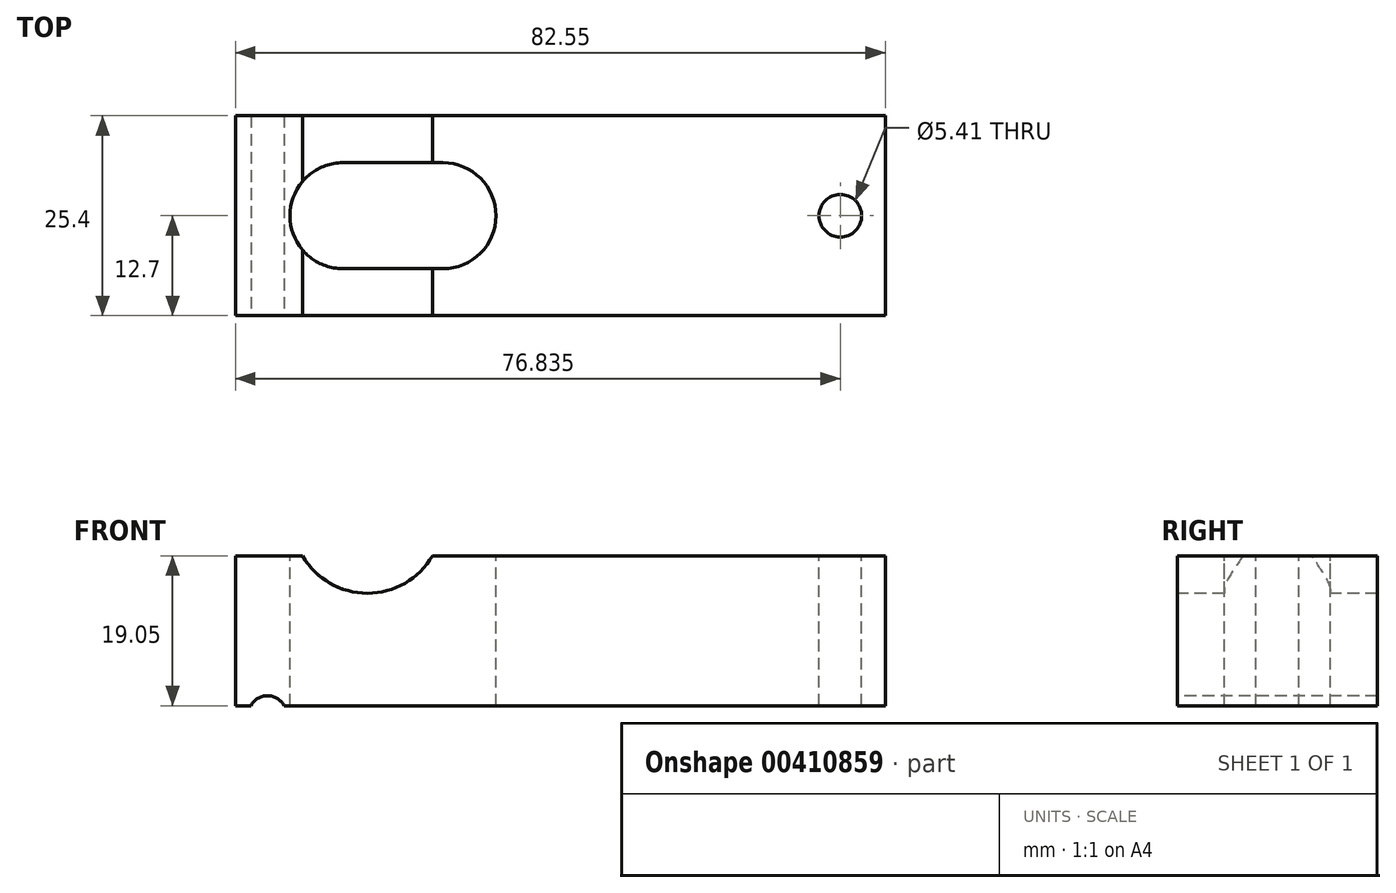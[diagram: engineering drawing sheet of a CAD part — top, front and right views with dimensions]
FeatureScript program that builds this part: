
annotation { "Feature Type Name" : "Feature", "Feature Type Description" : "" }
export const myFeature = defineFeature(function(context is Context, id is Id, definition is map)
    precondition{}
    {
        {
            var Q0;
            Q0=qCreatedBy(makeId("Front.planeOp"),FACE);
            var sketch = newSketch(context, id + "F0", { "sketchPlane" : qUnion([Q0])});
            skLineSegment(sketch, "E0.bottom", {"start": v(0, 0) * mm, "end": v(82.55, 0) * mm});
            skLineSegment(sketch, "E0.top", {"start": v(0, -19.05) * mm, "end": v(82.55, -19.05) * mm});
            skLineSegment(sketch, "E0.left", {"start": v(0, 0) * mm, "end": v(0, -19.05) * mm});
            skLineSegment(sketch, "E0.right", {"start": v(82.55, 0) * mm, "end": v(82.55, -19.05) * mm});
            skSolve(sketch);
        }
        {
            var Q0;
            Q0 = qSketchRegion(id + "F0", true);
            extrude(context, id + "F1", {"entities" : qUnion([Q0]), "depth" : 25.4 * mm});
        }
        {
            var Q0;
            Q0=makeQuery(id+"F1.opExtrude","SWEPT_FACE",FACE,{"disambiguationData":[OSD([sQuery(id+"F0.wireOp",EDGE,"E0.bottom")])]});
            var sketch = newSketch(context, id + "F2", { "sketchPlane" : qUnion([Q0])});
            skLineSegment(sketch, "E1", {"start": v(13.65, -12.7) * mm, "end": v(26.35, -12.7) * mm, "construction": true});
            skLineSegment(sketch, "E2", {"start": v(13.65, -5.97) * mm, "end": v(26.35, -5.97) * mm});
            skLineSegment(sketch, "E3", {"start": v(13.65, -19.43) * mm, "end": v(26.35, -19.43) * mm});
            skArc(sketch, "E4", {"start": v(13.65, -19.43) * mm, "mid": v(6.92, -12.7) * mm, "end": v(13.65, -5.97) * mm});
            skArc(sketch, "E5", {"start": v(26.35, -5.97) * mm, "mid": v(33.08, -12.7) * mm, "end": v(26.35, -19.43) * mm});
            skSolve(sketch);
        }
        {
            var Q0;
            Q0=makeQuery(id+"F2.imprint","IMPRINT",FACE,{"disambiguationData":[TD([[makeQuery(id+"F2.imprint","IMPRINT",EDGE,{"derivedFrom":sQuery(id+"F2.wireOp",EDGE,"E2")}),-1.0]])]});
            extrude(context, id + "F3", {"entities" : qUnion([Q0]), "operationType" : NewBodyOperationType.REMOVE, "oppositeDirection" : true, "depth" : 25.4 * mm});
        }
        {
            var Q0;
            Q0=makeQuery(id+"F1.opExtrude","CAP_FACE",FACE,{"disambiguationData":[OSD([sQuery(id+"F0.wireOp",EDGE,"E0.bottom"),sQuery(id+"F0.wireOp",EDGE,"E0.top"),sQuery(id+"F0.wireOp",EDGE,"E0.left"),sQuery(id+"F0.wireOp",EDGE,"E0.right")])],"isStart":false});
            var sketch = newSketch(context, id + "F4", { "sketchPlane" : qUnion([Q0])});
            skCircle(sketch, "E6", {"center": v(16.76, 4.76) * mm, "radius": 9.53 * mm});
            skSolve(sketch);
        }
        {
            var Q0;
            Q0 = qSketchRegion(id + "F4", true);
            extrude(context, id + "F5", {"entities" : qUnion([Q0]), "operationType" : NewBodyOperationType.REMOVE, "oppositeDirection" : true, "depth" : 25.4 * mm});
        }
        {
            var Q0;
            Q0=makeQuery(id+"F1.opExtrude","CAP_FACE",FACE,{"disambiguationData":[OSD([sQuery(id+"F0.wireOp",EDGE,"E0.bottom"),sQuery(id+"F0.wireOp",EDGE,"E0.top"),sQuery(id+"F0.wireOp",EDGE,"E0.left"),sQuery(id+"F0.wireOp",EDGE,"E0.right")])],"isStart":false});
            var sketch = newSketch(context, id + "F6", { "sketchPlane" : qUnion([Q0])});
            skCircle(sketch, "E7", {"center": v(4.06, -20.16) * mm, "radius": 2.38 * mm});
            skLineSegment(sketch, "E8", {"start": v(16.76, 5.67) * mm, "end": v(16.76, -20.55) * mm, "construction": true});
            skPoint(sketch, "E8.startSnap0", {"position": v(16.76, -4.76) * mm});
            skSolve(sketch);
        }
        {
            var Q0;
            Q0 = qSketchRegion(id + "F6", true);
            extrude(context, id + "F7", {"entities" : qUnion([Q0]), "operationType" : NewBodyOperationType.REMOVE, "oppositeDirection" : true, "depth" : 25.4 * mm});
        }
        {
            var Q0;
            {var subQ0=sQuery(id+"F0.wireOp",EDGE,"E0.right");var subQ3=sQuery(id+"F0.wireOp",EDGE,"E0.bottom");Q0=makeQuery(id+"F5.boolean.opBoolean","SPLIT",FACE,{"disambiguationData":[TD([makeQuery(id+"F1.opExtrude","SWEPT_FACE",FACE,{"disambiguationData":[OSD([subQ0])]})])],"derivedFrom":makeQuery(id+"F1.opExtrude","SWEPT_FACE",FACE,{"disambiguationData":[OSD([subQ3])]})});}
            var sketch = newSketch(context, id + "F8", { "sketchPlane" : qUnion([Q0])});
            skLineSegment(sketch, "E9", {"start": v(26.35, -12.7) * mm, "end": v(76.84, -12.7) * mm, "construction": true});
            skSolve(sketch);
        }
        {
            var Q0;
            Q0=sQuery(id+"F8.wireOp",VERTEX,"E9.end");
            var Q1;
            Q1=makeQuery(id+"F1.opExtrude","SWEPT_BODY",BODY,{"disambiguationData":[OSD([sQuery(id+"F0.wireOp",EDGE,"E0.bottom"),sQuery(id+"F0.wireOp",EDGE,"E0.top"),sQuery(id+"F0.wireOp",EDGE,"E0.left"),sQuery(id+"F0.wireOp",EDGE,"E0.right")])]});
            hole(context, id + "F9", {"style" : HoleStyle.SIMPLE, "endStyle" : HoleEndStyle.THROUGH, "standardTappedOrClearance" : lookupTablePath({ "standard" : "ANSI", "engagement" : "75%", "pitch" : "28 tpi", "size" : "1/4", "type" : "Tapped" }), "standardBlindInLast" : lookupTablePath({ "standard" : "ANSI", "engagement" : "75%", "pitch" : "28 tpi", "size" : "1/4", "type" : "Tapped" }), "holeDiameter" : 5.4 * mm, "showTappedDepth" : true, "isTappedThrough" : true, "tappedDepth" : 12.7 * mm, "tapClearance" : 3, "locations" : qUnion([Q0]), "scope" : qUnion([Q1]), "majorDiameter" : 6.35 * mm});
        }
    });
